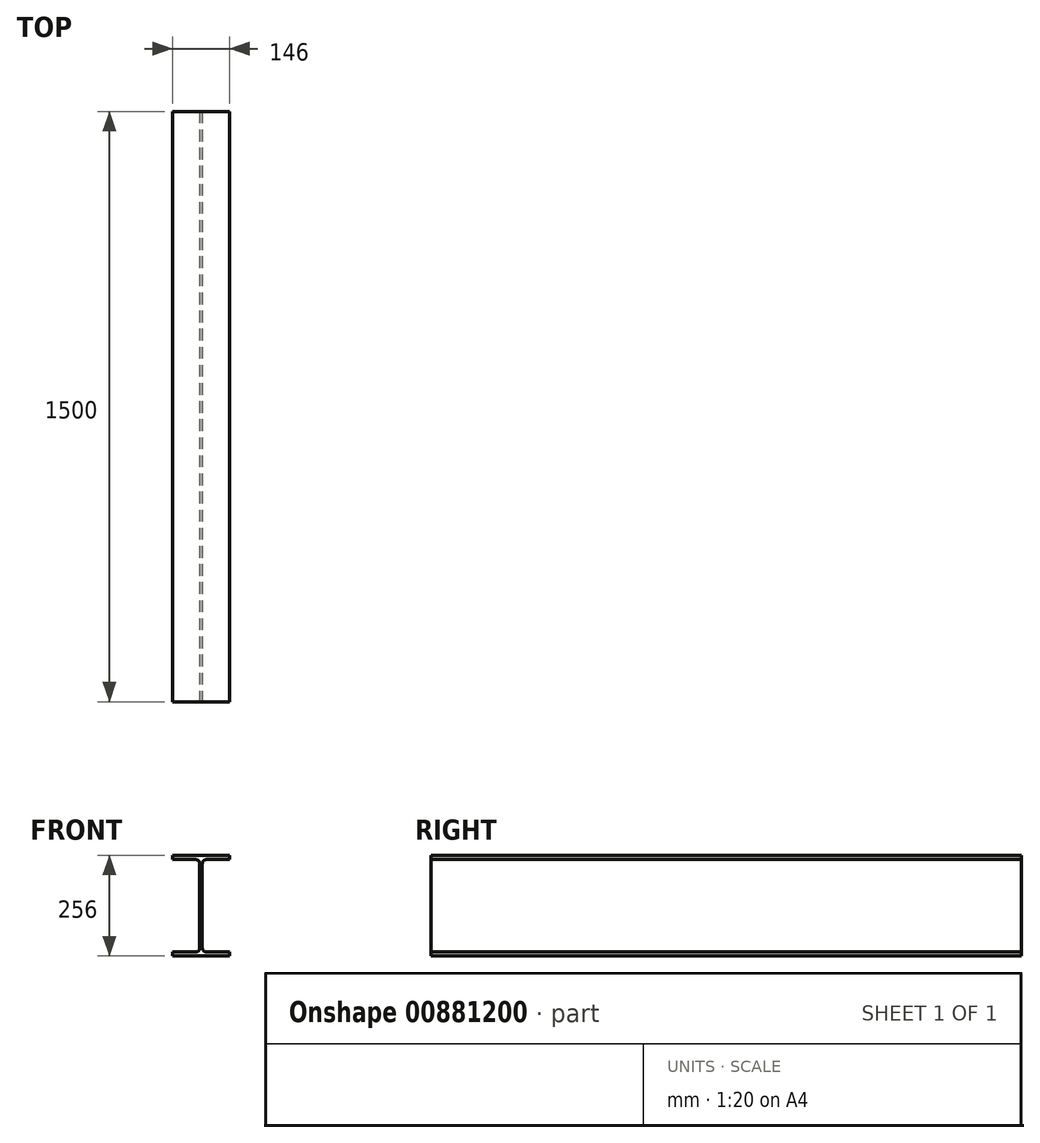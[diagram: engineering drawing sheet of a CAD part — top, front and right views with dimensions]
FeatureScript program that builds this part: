
annotation { "Feature Type Name" : "Feature", "Feature Type Description" : "" }
export const myFeature = defineFeature(function(context is Context, id is Id, definition is map)
    precondition{}
    {
        {
            var Q0;
            Q0=qCreatedBy(makeId("Front.planeOp"),FACE);
            var sketch = newSketch(context, id + "F0", { "sketchPlane" : qUnion([Q0])});
            skLineSegment(sketch, "E0", {"start": v(0, 147.9) * mm, "end": v(0, -157.79) * mm, "construction": true});
            skLineSegment(sketch, "E1", {"start": v(0, 108.32) * mm, "end": v(73, 108.32) * mm});
            skLineSegment(sketch, "E2", {"start": v(73, 108.32) * mm, "end": v(73, 97.42) * mm});
            skLineSegment(sketch, "E3", {"start": v(73, 97.42) * mm, "end": v(13.2, 97.42) * mm});
            skLineSegment(sketch, "E4", {"start": v(13.2, -136.78) * mm, "end": v(73, -136.78) * mm});
            skLineSegment(sketch, "E5", {"start": v(73, -136.78) * mm, "end": v(73, -147.68) * mm});
            skLineSegment(sketch, "E6", {"start": v(73, -147.68) * mm, "end": v(0, -147.68) * mm});
            skLineSegment(sketch, "E7", {"start": v(3.2, 87.42) * mm, "end": v(3.2, -126.78) * mm});
            skLineSegment(sketch, "E8.MirrorCS", {"start": v(0, 108.32) * mm, "end": v(-73, 108.32) * mm});
            skLineSegment(sketch, "E9.MirrorCS", {"start": v(-73, 108.32) * mm, "end": v(-73, 97.42) * mm});
            skLineSegment(sketch, "E10.MirrorCS", {"start": v(-73, 97.42) * mm, "end": v(-13.2, 97.42) * mm});
            skLineSegment(sketch, "E11.MirrorCS", {"start": v(-3.2, 87.42) * mm, "end": v(-3.2, -126.78) * mm});
            skLineSegment(sketch, "E12.MirrorCS", {"start": v(-13.2, -136.78) * mm, "end": v(-73, -136.78) * mm});
            skLineSegment(sketch, "E13.MirrorCS", {"start": v(-73, -136.78) * mm, "end": v(-73, -147.68) * mm});
            skLineSegment(sketch, "E14.MirrorCS", {"start": v(-73, -147.68) * mm, "end": v(0, -147.68) * mm});
            skPoint(sketch, "E15.visualSharp", {"position": v(3.2, 97.42) * mm});
            skArc(sketch, "E15.filletArc", {"start": v(13.2, 97.42) * mm, "mid": v(6.13, 94.5) * mm, "end": v(3.2, 87.42) * mm});
            skPoint(sketch, "E16.visualSharp", {"position": v(-3.2, 97.42) * mm});
            skArc(sketch, "E16.filletArc", {"start": v(-3.2, 87.42) * mm, "mid": v(-6.13, 94.5) * mm, "end": v(-13.2, 97.42) * mm});
            skPoint(sketch, "E17.visualSharp", {"position": v(-3.2, -136.78) * mm});
            skArc(sketch, "E17.filletArc", {"start": v(-13.2, -136.78) * mm, "mid": v(-6.13, -133.85) * mm, "end": v(-3.2, -126.78) * mm});
            skPoint(sketch, "E18.visualSharp", {"position": v(3.2, -136.78) * mm});
            skArc(sketch, "E18.filletArc", {"start": v(3.2, -126.78) * mm, "mid": v(6.13, -133.85) * mm, "end": v(13.2, -136.78) * mm});
            skSolve(sketch);
        }
        {
            var Q0;
            Q0=makeQuery(id+"F0.imprint","IMPRINT",FACE,{"disambiguationData":[TD([[makeQuery(id+"F0.imprint","IMPRINT",EDGE,{"derivedFrom":sQuery(id+"F0.wireOp",EDGE,"E1")}),-1.0]])]});
            extrude(context, id + "F1", {"entities" : qUnion([Q0]), "oppositeDirection" : true, "depth" : 1500 * mm, "offsetDistance" : 25 * mm});
        }
    });
